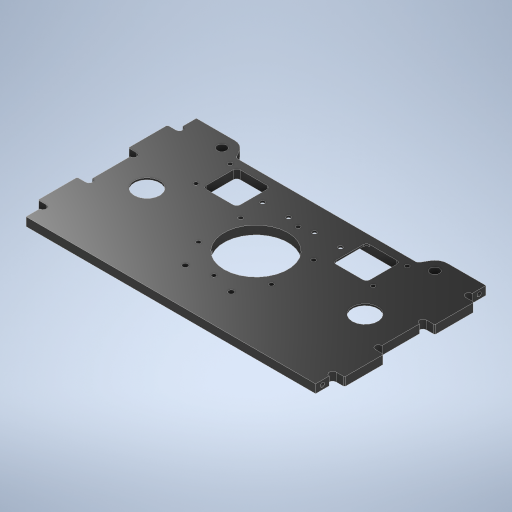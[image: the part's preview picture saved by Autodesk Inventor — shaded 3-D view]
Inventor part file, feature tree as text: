
AUTODESK INVENTOR PART (.ipt)
format: ipt  version: 2024.2 (Build 282272000, 272)  size: 794,112 bytes
history: native  units: mm
features: hole x5, sketch x3, extrude x3, chamfer x1, fillet x1
ambient origin geometry x8: Origin, YZ Plane, XZ Plane, XY Plane, X Axis, Y Axis, Z Axis, Center Point
bodies: Solid1 (feature_tree)
feature tree (13):
  sketch  "Sketch1"  dims[d0=100.0mm d1=180.0mm]
  extrude  "Extrusion1"  Depth=180.0mm
  extrude  "Extrusion2"  Depth=37.5mm
  extrude  "Extrusion3"  Depth=2.0mm
  hole  "Phi3.1"  [1 undecoded]
  hole  "Phi5.5"  [1 undecoded]
  hole  "Side-M3"  [1 undecoded]
  hole  "Phi2.5"  [1 undecoded]
  chamfer  "C0.5"  Distance=0.1mm
  hole  "Side-M2"  [1 undecoded]
  fillet  "Fillet2"  Radius=49.5mm
  sketch  "Sketch2"  dims[d2=37.5mm d3=43.0mm]
  sketch  "Sketch3"  dims[d4=32.0mm d5=27.0mm d6=27.0mm d7=9.5mm d8=8.5mm d9=0.1mm d10=0.1mm d13=60.0mm d15=360.0deg d17=49.5mm d18=5.0mm d19=30.0mm d20=12.0mm d21=2.0mm d22=6.0mm d23=8.0mm d24=58.0mm d25=15.0mm d26=10.0mm d27=140.0mm d29=125.0mm d32=5.0mm d33=0.0mm d34=2.0mm d35=0.0mm d36=2.459mm d37=6.0mm d38=4.0mm d39=2.0mm d40=90.0deg d41=6.0mm d42=0.0mm d43=3.1mm d44=6.0mm d45=4.0mm d46=2.0mm d47=90.0deg d48=8.0mm d49=0.0mm d50=5.5mm d51=6.0mm d52=4.0mm d53=2.0mm d54=90.0deg d55=8.0mm d56=0.0mm d57=2.459mm d58=6.0mm d59=4.0mm d60=2.0mm d61=90.0deg d62=6.0mm d63=0.0mm d64=2.0mm d66=0.5mm d67=2.0mm d68=45.0deg d77=2.0mm d78=17.7mm d79=17.7mm d80=0.5mm d81=76.2mm d93=4.0mm d94=0.0mm d100=4.0mm d101=32.0mm d102=2.459mm d103=6.0mm d104=4.0mm d105=2.0mm d106=90.0deg d107=4.0mm d108=0.0mm d128=8.5mm d130=29.5mm d131=25.0mm d132=98.0mm d133=2.0mm d134=4.0mm d135=20.0mm d138=0.5mm d139=6.0mm d140=2.0mm d141=2.0mm d142=2.459mm d143=6.0mm d144=4.0mm d145=2.0mm d146=90.0deg d147=8.0mm d148=20.594885mm d149=18.0mm d150=45.0mm d151=2.0mm d153=3.0mm d155=3.0mm d156=3.0mm d157=3.0mm d160=2.0mm d173=15.24mm d176=5.0mm d178=3.0mm d181=15.24mm d182=20.0mm d184=15.24mm d185=10.0mm d187=10.0mm d191=3.0mm d198=3.242mm d199=8.0mm d200=4.0mm d201=2.0mm d202=90.0deg d203=11.8mm d204=20.594885mm d205=5.0mm d212=2.0mm d213=3.0mm d215=4.0mm d216=3.0mm d218=60.0deg d221=7.5mm d223=2.0mm d225=15.0mm d226=21.0mm]
note: 5 required parameter values undecoded (feature->parameter linkage not recoverable at this tier; creation-order binding heuristic only, values carry confidence <= 0.55)
